FCSTD DOCUMENT  (FreeCAD 1.0R39319 (Git))
Label: Assy_Tee_Cam
License: All rights reserved
LicenseURL: https://en.wikipedia.org/wiki/All_rights_reserved
objects: App::DocumentObjectGroup×3, App::Link×3, PartDesign::CoordinateSystem×1, App::FeaturePython×1, App::Part×1
note: 1 computed .brp shape members not serialized (recipe doc carries the construction recipe); baked Part::Feature solids carry a one-line shape summary decoded from their .brp
EXTERNAL_REF file=Assy_Camera_Eyeball.FCStd obj=LCS_Origin
EXTERNAL_REF file=Assy_Camera_Eyeball.FCStd obj=Assembly
EXTERNAL_REF file=Assy_EyeScreen.FCStd obj=LCS_Origin
EXTERNAL_REF file=Assy_EyeScreen.FCStd obj=Assembly
EXTERNAL_REF file=Assy_EyeScreen_Clamp.FCStd obj=LCS_Origin
EXTERNAL_REF file=Assy_EyeScreen_Clamp.FCStd obj=Assembly

FEATURE [App::DocumentObjectGroup] Parts
FEATURE [PartDesign::CoordinateSystem] LCS_Origin
  AttacherType = Attacher::AttachEngine3D
  AttachmentSupport = -> [X_Axis]
  MapMode = 2
FEATURE [App::DocumentObjectGroup] Constraints
FEATURE [App::FeaturePython] Variables  # WARN: FeaturePython — macro-defined, semantics opaque (R4)
  Type = App::PropertyContainer
FEATURE [App::DocumentObjectGroup] Configurations
FEATURE [App::Link] Assy_Camera_Eyeball
  AttachedBy = #LCS_Origin
  AttachedTo = Parent Assembly#LCS_Origin
  LinkedObject = -> <external Assy_Camera_Eyeball.FCStd>#Assembly
  SolverId = Asm4EE
  expr: Placement = LCS_Origin.Placement * AttachmentOffset * Assy_Camera_Eyeball#LCS_Origin.Placement ^ -1
FEATURE [App::Link] Assy_EyeScreen
  AttachedBy = #LCS_Origin
  AttachedTo = Parent Assembly#LCS_Origin
  AttachmentOffset = pos=(0,0,0) rot=(0.57735,0.57735,-0.57735;4.18879rad)
  LinkPlacement = pos=(0,0,0) rot=(0.57735,0.57735,-0.57735;4.18879rad)
  LinkedObject = -> <external Assy_EyeScreen.FCStd>#Assembly
  Placement = pos=(0,0,0) rot=(0.57735,0.57735,-0.57735;4.18879rad)
  SolverId = Asm4EE
  expr: Placement = LCS_Origin.Placement * AttachmentOffset * Assy_EyeScreen#LCS_Origin.Placement ^ -1
FEATURE [App::Link] Assy_EyeScreen_Clamp
  AttachedBy = #LCS_Origin
  AttachedTo = Parent Assembly#LCS_Origin
  AttachmentOffset = pos=(0,0,0) rot=(-0.57735,-0.57735,0.57735;4.18879rad)
  LinkPlacement = pos=(0,0,0) rot=(-0.57735,-0.57735,0.57735;4.18879rad)
  LinkedObject = -> <external Assy_EyeScreen_Clamp.FCStd>#Assembly
  Placement = pos=(0,0,0) rot=(-0.57735,-0.57735,0.57735;4.18879rad)
  SolverId = Asm4EE
  expr: Placement = LCS_Origin.Placement * AttachmentOffset * Assy_EyeScreen_Clamp#LCS_Origin.Placement ^ -1
FEATURE [App::Part] Assembly  label="Assy_Tee_Cam"
  AssemblyType = Part::Link
  Group = -> [LCS_Origin,Constraints,Variables,Configurations,Assy_Camera_Eyeball,Assy_EyeScreen,Assy_EyeScreen_Clamp]
  Origin = -> Origin
  Type = Assembly
